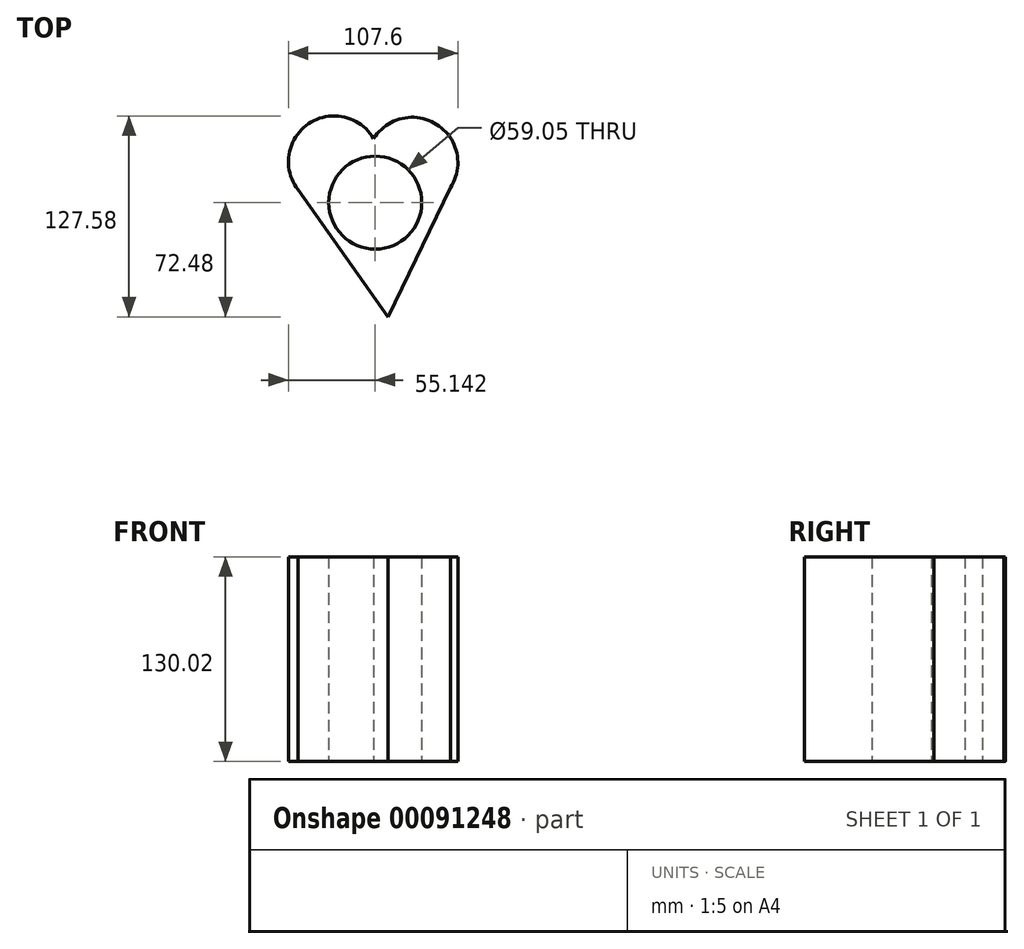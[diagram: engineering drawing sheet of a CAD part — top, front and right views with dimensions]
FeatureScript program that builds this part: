
annotation { "Feature Type Name" : "Feature", "Feature Type Description" : "" }
export const myFeature = defineFeature(function(context is Context, id is Id, definition is map)
    precondition{}
    {
        {
            var Q0;
            Q0=qCreatedBy(makeId("Top.planeOp"),FACE);
            var sketch = newSketch(context, id + "F0", { "sketchPlane" : qUnion([Q0])});
            skArc(sketch, "E0", {"start": v(-9.2, 45.4) * mm, "mid": v(-50.56, 54.87) * mm, "end": v(-57.2, 12.97) * mm});
            skArc(sketch, "E1", {"start": v(39.61, 14.33) * mm, "mid": v(30.86, 54.47) * mm, "end": v(-9.2, 45.4) * mm});
            skLineSegment(sketch, "E2", {"start": v(-58.74, 15.13) * mm, "end": v(0, -67.73) * mm});
            skLineSegment(sketch, "E3", {"start": v(39.61, 14.33) * mm, "end": v(0, -67.73) * mm});
            skCircle(sketch, "E4", {"center": v(-8.2, 4.75) * mm, "radius": 29.53 * mm});
            skSolve(sketch);
        }
        {
            var Q0;
            Q0 = qSketchRegion(id + "F0", true);
            extrude(context, id + "F1", {"entities" : qUnion([Q0]), "depth" : 130.02 * mm});
        }
    });
